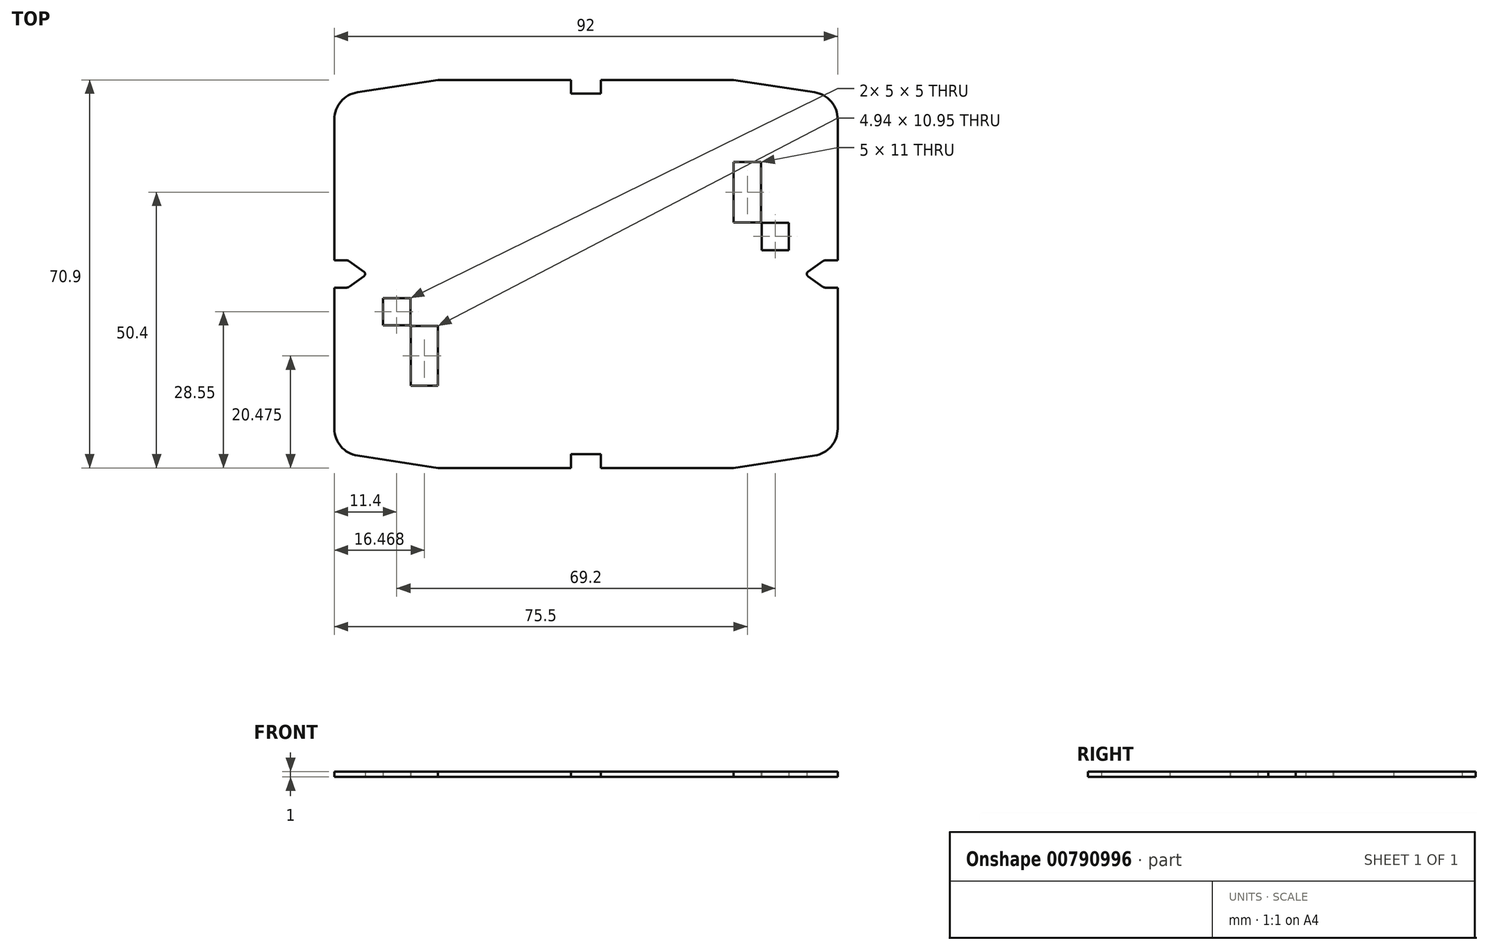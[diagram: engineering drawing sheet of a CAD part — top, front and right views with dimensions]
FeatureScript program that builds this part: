
annotation { "Feature Type Name" : "Feature", "Feature Type Description" : "" }
export const myFeature = defineFeature(function(context is Context, id is Id, definition is map)
    precondition{}
    {
        {
            var Q0;
            Q0=qCreatedBy(makeId("Top.planeOp"),FACE);
            var sketch = newSketch(context, id + "F0", { "sketchPlane" : qUnion([Q0])});
            skLineSegment(sketch, "E0.left", {"start": v(46, -28.27) * mm, "end": v(46, -2.5) * mm});
            skLineSegment(sketch, "E0.right", {"start": v(-46, -28.27) * mm, "end": v(-46, -2.5) * mm});
            skPoint(sketch, "E0.middle", {"position": v(0, 0) * mm});
            skLineSegment(sketch, "E1", {"start": v(-46, 0) * mm, "end": v(46, 0) * mm, "construction": true});
            skLineSegment(sketch, "E2", {"start": v(0, 35.45) * mm, "end": v(0, -35.45) * mm, "construction": true});
            skLineSegment(sketch, "E3.top", {"start": v(32, 20.45) * mm, "end": v(27, 20.45) * mm});
            skLineSegment(sketch, "E3.left", {"start": v(32, 9.45) * mm, "end": v(32, 20.45) * mm});
            skLineSegment(sketch, "E3.right", {"start": v(27, 9.45) * mm, "end": v(27, 20.45) * mm});
            skPoint(sketch, "E3.middle", {"position": v(29.5, 14.95) * mm});
            skLineSegment(sketch, "E4.MirrorCS", {"start": v(46, 0) * mm, "end": v(-46, 0) * mm, "construction": true});
            skLineSegment(sketch, "E5.MirrorCS", {"start": v(-27.06, -9.5) * mm, "end": v(-27.06, -20.45) * mm});
            skLineSegment(sketch, "E6.MirrorCS", {"start": v(-32, -9.45) * mm, "end": v(-32, -20.45) * mm});
            skLineSegment(sketch, "E7.MirrorCS", {"start": v(-32.06, -20.45) * mm, "end": v(-27.06, -20.45) * mm});
            skPoint(sketch, "E8.middle", {"position": v(0, 35.45) * mm});
            skLineSegment(sketch, "E9", {"start": v(-2.75, 35.45) * mm, "end": v(-2.75, 32.95) * mm});
            skLineSegment(sketch, "E10", {"start": v(-2.75, 32.95) * mm, "end": v(0, 32.95) * mm});
            skLineSegment(sketch, "E11.trimOffspring", {"start": v(-2.75, 35.45) * mm, "end": v(-27.06, 35.45) * mm});
            skLineSegment(sketch, "E12.MirrorCS", {"start": v(2.75, 35.45) * mm, "end": v(2.75, 32.95) * mm});
            skLineSegment(sketch, "E13.MirrorCS", {"start": v(2.75, 32.95) * mm, "end": v(0, 32.95) * mm});
            skLineSegment(sketch, "E14.MirrorCS", {"start": v(-2.75, -35.45) * mm, "end": v(-2.75, -32.95) * mm});
            skLineSegment(sketch, "E15.MirrorCS", {"start": v(-2.75, -32.95) * mm, "end": v(0, -32.95) * mm});
            skLineSegment(sketch, "E16.MirrorCS", {"start": v(2.75, -32.95) * mm, "end": v(0, -32.95) * mm});
            skLineSegment(sketch, "E17.MirrorCS", {"start": v(2.75, -35.45) * mm, "end": v(2.75, -32.95) * mm});
            skLineSegment(sketch, "E18.trimOffspring", {"start": v(-2.75, -35.45) * mm, "end": v(-27.06, -35.45) * mm});
            skLineSegment(sketch, "E19", {"start": v(-46, -2.5) * mm, "end": v(-43.82, -2.5) * mm});
            skLineSegment(sketch, "E20.trimOffspring", {"start": v(-46, 2.5) * mm, "end": v(-46, 28.27) * mm});
            skPoint(sketch, "E21", {"position": v(-40, 0) * mm});
            skLineSegment(sketch, "E22", {"start": v(-43.24, -2.31) * mm, "end": v(-40.57, -0.4) * mm});
            skLineSegment(sketch, "E23.MirrorCS", {"start": v(-46, 2.5) * mm, "end": v(-43.82, 2.5) * mm});
            skLineSegment(sketch, "E24.MirrorCS", {"start": v(-43.24, 2.31) * mm, "end": v(-40.57, 0.4) * mm});
            skPoint(sketch, "E25.visualSharp", {"position": v(-43.5, 2.5) * mm});
            skArc(sketch, "E25.filletArc", {"start": v(-43.24, 2.31) * mm, "mid": v(-43.52, 2.45) * mm, "end": v(-43.82, 2.5) * mm});
            skPoint(sketch, "E26.visualSharp", {"position": v(-43.5, -2.5) * mm});
            skArc(sketch, "E26.filletArc", {"start": v(-43.82, -2.5) * mm, "mid": v(-43.52, -2.45) * mm, "end": v(-43.24, -2.31) * mm});
            skArc(sketch, "E27.filletArc", {"start": v(-40.57, -0.4) * mm, "mid": v(-40.36, 0) * mm, "end": v(-40.57, 0.4) * mm});
            skLineSegment(sketch, "E28.MirrorCS", {"start": v(46, 2.5) * mm, "end": v(43.82, 2.5) * mm});
            skArc(sketch, "E29.MirrorCS", {"start": v(43.24, 2.31) * mm, "mid": v(43.52, 2.45) * mm, "end": v(43.82, 2.5) * mm});
            skLineSegment(sketch, "E30.MirrorCS", {"start": v(43.24, 2.31) * mm, "end": v(40.57, 0.4) * mm});
            skArc(sketch, "E31.MirrorCS", {"start": v(40.57, -0.4) * mm, "mid": v(40.36, 0) * mm, "end": v(40.57, 0.4) * mm});
            skLineSegment(sketch, "E32.MirrorCS", {"start": v(43.24, -2.31) * mm, "end": v(40.57, -0.4) * mm});
            skArc(sketch, "E33.MirrorCS", {"start": v(43.82, -2.5) * mm, "mid": v(43.52, -2.45) * mm, "end": v(43.24, -2.31) * mm});
            skLineSegment(sketch, "E34.MirrorCS", {"start": v(46, -2.5) * mm, "end": v(43.82, -2.5) * mm});
            skLineSegment(sketch, "E35.trimOffspring", {"start": v(46, 2.5) * mm, "end": v(46, 28.27) * mm});
            skPoint(sketch, "E36.visualSharp", {"position": v(-46, -35.45) * mm});
            skPoint(sketch, "E37.visualSharp", {"position": v(46, -35.45) * mm});
            skPoint(sketch, "E38.visualSharp", {"position": v(46, 35.45) * mm});
            skPoint(sketch, "E39.visualSharp", {"position": v(-46, 35.45) * mm});
            skLineSegment(sketch, "E39.filletArc", {"start": v(-46, 35.45) * mm, "end": v(-46, 35.45) * mm});
            skLineSegment(sketch, "E40", {"start": v(27, 9.45) * mm, "end": v(32, 9.45) * mm});
            skLineSegment(sketch, "E41", {"start": v(-32, -9.5) * mm, "end": v(-27.06, -9.5) * mm});
            skLineSegment(sketch, "E42.bottom", {"start": v(-32.1, -9.4) * mm, "end": v(-37.1, -9.4) * mm});
            skLineSegment(sketch, "E42.top", {"start": v(-32.1, -4.4) * mm, "end": v(-37.1, -4.4) * mm});
            skLineSegment(sketch, "E42.left", {"start": v(-32.1, -9.4) * mm, "end": v(-32.1, -4.4) * mm});
            skLineSegment(sketch, "E42.right", {"start": v(-37.1, -9.4) * mm, "end": v(-37.1, -4.4) * mm});
            skPoint(sketch, "E42.middle", {"position": v(-34.6, -6.9) * mm});
            skLineSegment(sketch, "E43.bottom", {"start": v(37.1, 4.35) * mm, "end": v(32.1, 4.35) * mm});
            skLineSegment(sketch, "E43.top", {"start": v(37.1, 9.35) * mm, "end": v(32.1, 9.35) * mm});
            skLineSegment(sketch, "E43.left", {"start": v(37.1, 4.35) * mm, "end": v(37.1, 9.35) * mm});
            skLineSegment(sketch, "E43.right", {"start": v(32.1, 4.35) * mm, "end": v(32.1, 9.35) * mm});
            skPoint(sketch, "E43.middle", {"position": v(34.6, 6.85) * mm});
            skLineSegment(sketch, "E44", {"start": v(27, 35.45) * mm, "end": v(27, -35.45) * mm, "construction": true});
            skLineSegment(sketch, "E45", {"start": v(-27.06, -35.45) * mm, "end": v(-27.06, 35.45) * mm, "construction": true});
            skLineSegment(sketch, "E46", {"start": v(27, -35.45) * mm, "end": v(2.75, -35.45) * mm});
            skLineSegment(sketch, "E47", {"start": v(27, 35.45) * mm, "end": v(2.75, 35.45) * mm});
            skLineSegment(sketch, "E48.0", {"start": v(-5.5, 32.95) * mm, "end": v(-27.06, 32.95) * mm, "construction": true});
            skLineSegment(sketch, "E48.1", {"start": v(-5.5, 32.95) * mm, "end": v(-5.5, 30.95) * mm, "construction": true});
            skLineSegment(sketch, "E48.2", {"start": v(-5.5, 30.95) * mm, "end": v(0, 30.95) * mm, "construction": true});
            skLineSegment(sketch, "E48.3", {"start": v(5.5, 30.95) * mm, "end": v(0, 30.95) * mm, "construction": true});
            skLineSegment(sketch, "E48.4", {"start": v(5.5, 32.95) * mm, "end": v(5.5, 30.95) * mm, "construction": true});
            skLineSegment(sketch, "E48.5", {"start": v(-27.06, 32.95) * mm, "end": v(-43.5, 32.95) * mm, "construction": true});
            skLineSegment(sketch, "E48.6", {"start": v(27, 32.95) * mm, "end": v(5.5, 32.95) * mm, "construction": true});
            skLineSegment(sketch, "E48.7", {"start": v(43.5, 32.95) * mm, "end": v(27, 32.95) * mm, "construction": true});
            skLineSegment(sketch, "E48.8", {"start": v(43.5, 1.43) * mm, "end": v(43.5, 32.95) * mm, "construction": true});
            skArc(sketch, "E48.9", {"start": v(43.5, -1.43) * mm, "mid": v(37.86, 0) * mm, "end": v(43.5, 1.43) * mm, "construction": true});
            skLineSegment(sketch, "E48.10", {"start": v(43.5, -32.95) * mm, "end": v(43.5, -1.43) * mm, "construction": true});
            skLineSegment(sketch, "E48.11", {"start": v(43.5, -32.95) * mm, "end": v(27, -32.95) * mm, "construction": true});
            skLineSegment(sketch, "E48.12", {"start": v(-27.06, -32.95) * mm, "end": v(-43.5, -32.95) * mm, "construction": true});
            skLineSegment(sketch, "E48.13", {"start": v(-43.5, -32.95) * mm, "end": v(-43.5, -1.43) * mm, "construction": true});
            skArc(sketch, "E48.14", {"start": v(-43.5, -1.43) * mm, "mid": v(-37.86, 0) * mm, "end": v(-43.5, 1.43) * mm, "construction": true});
            skLineSegment(sketch, "E48.15", {"start": v(-43.5, 1.43) * mm, "end": v(-43.5, 32.95) * mm, "construction": true});
            skLineSegment(sketch, "E48.16", {"start": v(-5.5, -32.95) * mm, "end": v(-27.06, -32.95) * mm, "construction": true});
            skLineSegment(sketch, "E48.17", {"start": v(-5.5, -32.95) * mm, "end": v(-5.5, -30.95) * mm, "construction": true});
            skLineSegment(sketch, "E48.18", {"start": v(-5.5, -30.95) * mm, "end": v(0, -30.95) * mm, "construction": true});
            skLineSegment(sketch, "E48.19", {"start": v(5.5, -30.95) * mm, "end": v(0, -30.95) * mm, "construction": true});
            skLineSegment(sketch, "E48.20", {"start": v(5.5, -32.95) * mm, "end": v(5.5, -30.95) * mm, "construction": true});
            skLineSegment(sketch, "E48.21", {"start": v(27, -32.95) * mm, "end": v(5.5, -32.95) * mm, "construction": true});
            skLineSegment(sketch, "E49", {"start": v(-41.75, 33.22) * mm, "end": v(-27.06, 35.45) * mm, "construction": true});
            skLineSegment(sketch, "E50", {"start": v(-41.75, -33.22) * mm, "end": v(-27.06, -35.45) * mm, "construction": true});
            skLineSegment(sketch, "E51", {"start": v(27, -35.45) * mm, "end": v(41.75, -33.22) * mm, "construction": true});
            skLineSegment(sketch, "E52", {"start": v(27, 35.45) * mm, "end": v(41.75, 33.22) * mm, "construction": true});
            skPoint(sketch, "E53.visualSharp", {"position": v(-46, 32.57) * mm});
            skArc(sketch, "E53.filletArc", {"start": v(-41.75, 33.22) * mm, "mid": v(-44.8, 31.53) * mm, "end": v(-46, 28.27) * mm});
            skPoint(sketch, "E54.visualSharp", {"position": v(-46, -32.57) * mm});
            skArc(sketch, "E54.filletArc", {"start": v(-46, -28.27) * mm, "mid": v(-44.8, -31.53) * mm, "end": v(-41.75, -33.22) * mm});
            skPoint(sketch, "E55.visualSharp", {"position": v(46, -32.57) * mm});
            skArc(sketch, "E55.filletArc", {"start": v(41.75, -33.22) * mm, "mid": v(44.8, -31.53) * mm, "end": v(46, -28.27) * mm});
            skPoint(sketch, "E56.visualSharp", {"position": v(46, 32.57) * mm});
            skArc(sketch, "E56.filletArc", {"start": v(46, 28.27) * mm, "mid": v(44.8, 31.53) * mm, "end": v(41.75, 33.22) * mm});
            skLineSegment(sketch, "E57", {"start": v(-41.75, 33.22) * mm, "end": v(-27.06, 35.45) * mm});
            skLineSegment(sketch, "E58", {"start": v(27, 35.45) * mm, "end": v(41.75, 33.22) * mm});
            skLineSegment(sketch, "E59", {"start": v(-27.06, -35.45) * mm, "end": v(-41.75, -33.22) * mm});
            skLineSegment(sketch, "E60", {"start": v(27, -35.45) * mm, "end": v(41.75, -33.22) * mm});
            skSolve(sketch);
        }
        {
            var Q0;
            Q0=makeQuery(id+"F0.imprint","IMPRINT",FACE,{"disambiguationData":[TD([[makeQuery(id+"F0.imprint","IMPRINT",EDGE,{"derivedFrom":sQuery(id+"F0.wireOp",EDGE,"E0.left")}),1.0]])]});
            extrude(context, id + "F1", {"entities" : qUnion([Q0]), "depth" : 1 * mm, "offsetDistance" : 25 * mm});
        }
    });
